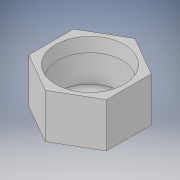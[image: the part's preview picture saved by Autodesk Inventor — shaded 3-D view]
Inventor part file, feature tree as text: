
AUTODESK INVENTOR PART (.ipt)
format: ipt  version: 2019.4 (Build 234330000, 330)  size: 109,056 bytes
history: native  units: in
note: dims shown in document units (in); Inventor stores cm internally (conversion verified against a paired STEP export)
features: extrude x2, sketch x2, chamfer x1
ambient origin geometry x8: Origin, YZ Plane, XZ Plane, XY Plane, X Axis, Y Axis, Z Axis, Center Point
bodies: Solid1 (feature_tree)
feature tree (5):
  extrude  "Extrusion1"  Depth=0.7874in TaperAngle=0.0deg
  extrude  "Extrusion2"  Depth=0.7087in TaperAngle=0.0deg
  chamfer  "Chamfer1"  Distance=0.0787in
  sketch  "Sketch1"  dims[d0=1.378in d1=0.7874in d2=0.0in]
  sketch  "Sketch2"  dims[d3=1.1417in d4=0.7087in d5=0.0in d6=0.0394in d7=0.0787in d8=0.5497in]
